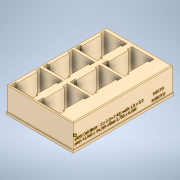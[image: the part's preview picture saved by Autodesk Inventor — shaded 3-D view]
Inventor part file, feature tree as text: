
AUTODESK INVENTOR PART (.ipt)
format: ipt  version: 2020 (Build 240168000, 168)  size: 2,566,144 bytes
history: native  units: in
note: dims shown in document units (in); Inventor stores cm internally (conversion verified against a paired STEP export)
features: extrude x3, sketch x3, fillet x1, pattern_linear x1, emboss x1
ambient origin geometry x8: Origin, YZ Plane, XZ Plane, XY Plane, X Axis, Y Axis, Z Axis, Center Point
bodies: Solid1 (feature_tree)
feature tree (9):
  extrude  "Extrusion1"  TaperAngle=45.0deg  [1 undecoded]
  extrude  "Extrusion2"  TaperAngle=225.0deg  [1 undecoded]
  extrude  "Extrusion3"  Depth=0.0394in TaperAngle=0.0deg
  fillet  "Fillet1"  Radius=0.1969in
  pattern_linear  "Rectangular Pattern2"  Spacing1=0.0in  [1 undecoded]
  emboss  "Emboss2"
  sketch  "Sketch1"  dims[d3=0.0in d5=45.0deg]
  sketch  "Sketch2"  dims[d6=0.0394in d7=225.0deg]
  sketch  "Sketch5"  dims[d9=0.0in d48=0.0394in d49=0.0in d51=0.1969in d55=0.0in d56=0.7874in d58=1.3527in d59=1.1811in d61=1.6143in d63=0.0689in d64=0.959in d65=1.4765in d68=0.0787in d69=0.2362in d70=0.0787in d71=0.2362in d72=0.0787in d73=0.2362in]
note: 3 required parameter values undecoded (feature->parameter linkage not recoverable at this tier; creation-order binding heuristic only, values carry confidence <= 0.55)
